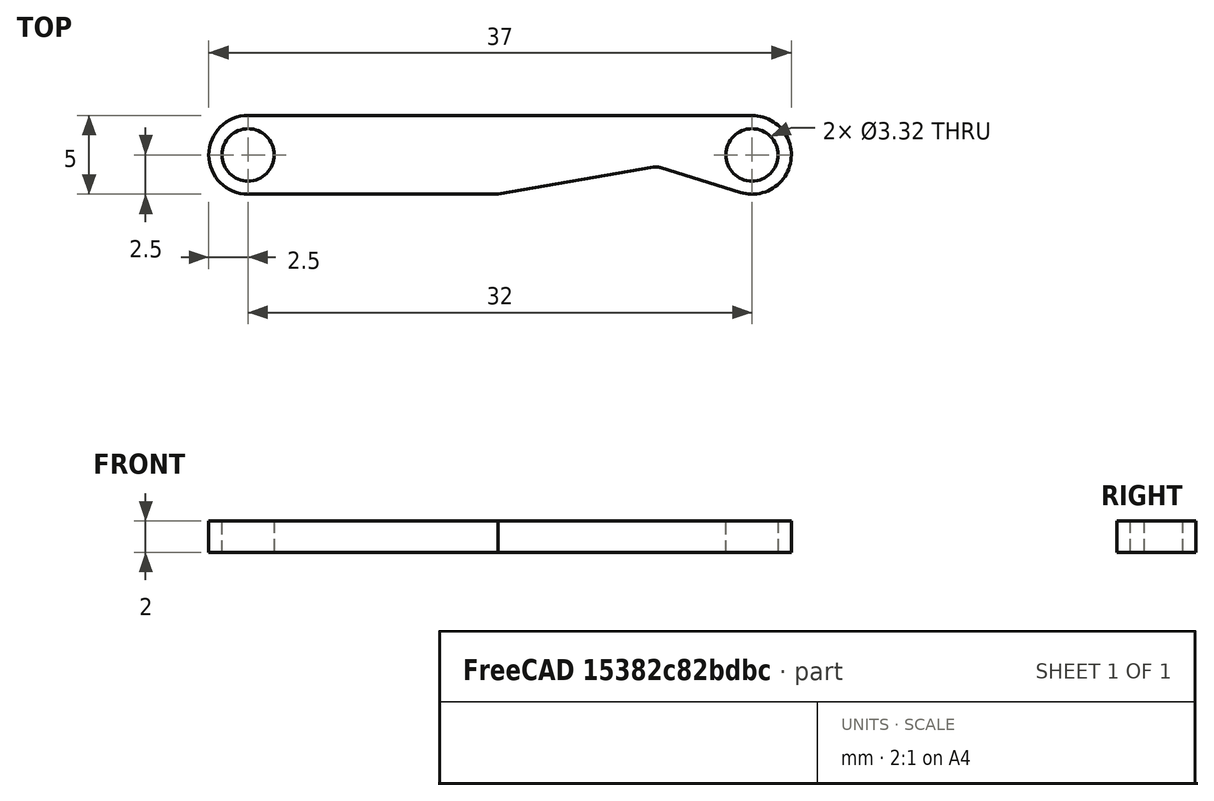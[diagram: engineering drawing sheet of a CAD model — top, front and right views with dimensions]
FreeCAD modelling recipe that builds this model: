
FCSTD DOCUMENT  (FreeCAD 1.0R39285 (Git))
Label: TransferLinkageRight
License: All rights reserved
LicenseURL: https://en.wikipedia.org/wiki/All_rights_reserved
objects: PartDesign::SubShapeBinder×1, Part::Mirroring×1, App::Part×1
note: 2 computed .brp shape members not serialized (recipe doc carries the construction recipe); baked Part::Feature solids carry a one-line shape summary decoded from their .brp
EXTERNAL_REF file=TransferLinkageLeft.FCStd obj=Part

FEATURE [PartDesign::SubShapeBinder] Binder  label="TransferLinkageLeftBody"
  BindCopyOnChange = 0
  BindMode = 0
  ClaimChildren = false
  Context = -> Part [Binder.]
  Fuse = false
  MakeFace = true
  OffsetFill = false
  OffsetIntersection = false
  OffsetJoinType = 0
  OffsetOpenResult = false
  PartialLoad = false
  Refine = true
  Relative = true
  Support = -> [<external TransferLinkageLeft.FCStd>#Part[Body.]]
  _Version = 2
FEATURE [Part::Mirroring] Part__Mirroring  label="TransferLinkageRightBody"
  Base = (0,0,0)
  Normal = (1,0,0)
  Source = -> Binder
FEATURE [App::Part] Part  label="TransferLinkageRightPart"
  Group = -> [Binder,Part__Mirroring]
  Origin = -> Origin
